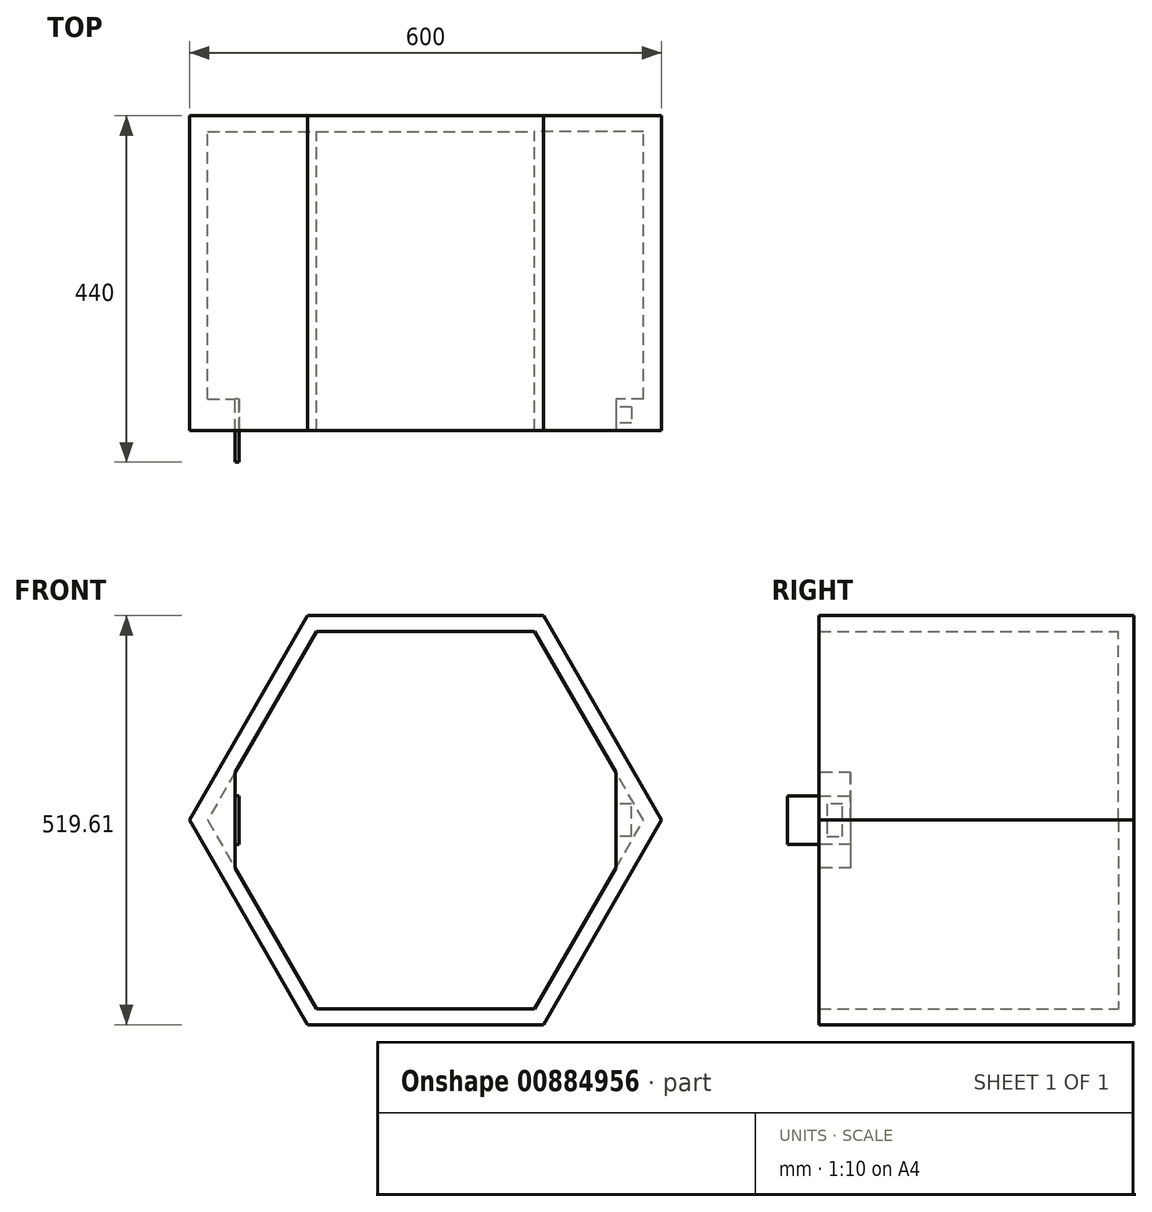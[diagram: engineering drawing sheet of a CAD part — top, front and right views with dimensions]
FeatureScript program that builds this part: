
annotation { "Feature Type Name" : "Feature", "Feature Type Description" : "" }
export const myFeature = defineFeature(function(context is Context, id is Id, definition is map)
    precondition{}
    {
        {
            var Q0;
            Q0=qCreatedBy(makeId("Front.planeOp"),FACE);
            var sketch = newSketch(context, id + "F0", { "sketchPlane" : qUnion([Q0])});
            skLineSegment(sketch, "E0", {"start": v(-124.49, 79.77) * mm, "end": v(175.51, 79.77) * mm});
            skLineSegment(sketch, "E1", {"start": v(-124.49, 79.77) * mm, "end": v(-274.49, -180.04) * mm});
            skLineSegment(sketch, "E2", {"start": v(-274.49, -180.04) * mm, "end": v(-124.49, -439.84) * mm});
            skLineSegment(sketch, "E3", {"start": v(-124.49, -439.84) * mm, "end": v(175.51, -439.84) * mm});
            skLineSegment(sketch, "E4", {"start": v(175.51, -439.84) * mm, "end": v(325.51, -180.04) * mm});
            skLineSegment(sketch, "E5", {"start": v(325.51, -180.04) * mm, "end": v(175.51, 79.77) * mm});
            skSolve(sketch);
        }
        {
            var Q0;
            Q0=makeQuery(id+"F0.imprint","IMPRINT",FACE,{"disambiguationData":[TD([[makeQuery(id+"F0.imprint","IMPRINT",EDGE,{"derivedFrom":sQuery(id+"F0.wireOp",EDGE,"E0")}),-1.0]])]});
            extrude(context, id + "F1", {"entities" : qUnion([Q0]), "depth" : 400 * mm, "offsetDistance" : 25.4 * mm});
        }
        {
            var Q0;
            Q0=makeQuery(id+"F1.opExtrude","CAP_FACE",FACE,{"disambiguationData":[OSD([sQuery(id+"F0.wireOp",EDGE,"E0"),sQuery(id+"F0.wireOp",EDGE,"E1"),sQuery(id+"F0.wireOp",EDGE,"E2"),sQuery(id+"F0.wireOp",EDGE,"E3"),sQuery(id+"F0.wireOp",EDGE,"E4"),sQuery(id+"F0.wireOp",EDGE,"E5")])],"isStart":false});
            shell(context, id + "F2", {"entities" : qUnion([Q0]), "thickness" : 20 * mm});
        }
        {
            var Q0;
            Q0=makeQuery(id+"F1.opExtrude","CAP_FACE",FACE,{"disambiguationData":[OSD([sQuery(id+"F0.wireOp",EDGE,"E0"),sQuery(id+"F0.wireOp",EDGE,"E1"),sQuery(id+"F0.wireOp",EDGE,"E2"),sQuery(id+"F0.wireOp",EDGE,"E3"),sQuery(id+"F0.wireOp",EDGE,"E4"),sQuery(id+"F0.wireOp",EDGE,"E5")])],"isStart":false});
            var sketch = newSketch(context, id + "F3", { "sketchPlane" : qUnion([Q0])});
            skLineSegment(sketch, "E6", {"start": v(-251.4, -180.04) * mm, "end": v(-216.4, -119.41) * mm});
            skLineSegment(sketch, "E7", {"start": v(-216.4, -119.41) * mm, "end": v(-216.4, -240.66) * mm});
            skLineSegment(sketch, "E8", {"start": v(-216.4, -240.66) * mm, "end": v(-251.4, -180.04) * mm});
            skLineSegment(sketch, "E9", {"start": v(302.42, -180.04) * mm, "end": v(267.42, -119.41) * mm});
            skLineSegment(sketch, "E10", {"start": v(267.42, -119.41) * mm, "end": v(267.42, -240.66) * mm});
            skLineSegment(sketch, "E11", {"start": v(267.42, -240.66) * mm, "end": v(302.42, -180.04) * mm});
            skSolve(sketch);
        }
        {
            var Q0;
            Q0=makeQuery(id+"F3.imprint","IMPRINT",FACE,{"disambiguationData":[TD([[makeQuery(id+"F3.imprint","IMPRINT",EDGE,{"derivedFrom":sQuery(id+"F3.wireOp",EDGE,"E9")}),1.0]])]});
            var Q1;
            Q1=makeQuery(id+"F3.imprint","IMPRINT",FACE,{"disambiguationData":[TD([[makeQuery(id+"F3.imprint","IMPRINT",EDGE,{"derivedFrom":sQuery(id+"F3.wireOp",EDGE,"E6")}),1.0]])]});
            extrude(context, id + "F4", {"entities" : qUnion([Q0, Q1]), "operationType" : NewBodyOperationType.ADD, "oppositeDirection" : true, "depth" : 40 * mm, "offsetDistance" : 25.4 * mm});
        }
        {
            var Q0;
            Q0=makeQuery(id+"F4.opExtrude","SWEPT_FACE",FACE,{"disambiguationData":[OSD([sQuery(id+"F3.wireOp",EDGE,"E7")])]});
            var sketch = newSketch(context, id + "F5", { "sketchPlane" : qUnion([Q0])});
            skLineSegment(sketch, "E12", {"start": v(-400, -149.41) * mm, "end": v(-360, -149.41) * mm});
            skLineSegment(sketch, "E13", {"start": v(-360, -149.41) * mm, "end": v(-360, -210.66) * mm});
            skLineSegment(sketch, "E14", {"start": v(-360, -210.66) * mm, "end": v(-400, -210.66) * mm});
            skLineSegment(sketch, "E15", {"start": v(-400, -210.66) * mm, "end": v(-400, -149.41) * mm});
            skSolve(sketch);
        }
        {
            var Q0;
            Q0 = qSketchRegion(id + "F5", true);
            extrude(context, id + "F6", {"entities" : qUnion([Q0]), "operationType" : NewBodyOperationType.ADD, "depth" : 5 * mm, "offsetDistance" : 25.4 * mm});
        }
        {
            var Q0;
            Q0=makeQuery(id+"F6.boolean.opBoolean","MERGE",FACE,{"derivedFrom":[makeQuery(id+"F4.boolean.opBoolean","MERGE",FACE,{"derivedFrom":[makeQuery(id+"F1.opExtrude","CAP_FACE",FACE,{"disambiguationData":[OSD([sQuery(id+"F0.wireOp",EDGE,"E0"),sQuery(id+"F0.wireOp",EDGE,"E1"),sQuery(id+"F0.wireOp",EDGE,"E2"),sQuery(id+"F0.wireOp",EDGE,"E3"),sQuery(id+"F0.wireOp",EDGE,"E4"),sQuery(id+"F0.wireOp",EDGE,"E5")])],"isStart":false}),makeQuery(id+"F4.opExtrude","CAP_FACE",FACE,{"disambiguationData":[OSD([sQuery(id+"F3.wireOp",EDGE,"E6"),sQuery(id+"F3.wireOp",EDGE,"E7"),sQuery(id+"F3.wireOp",EDGE,"E8")])],"isStart":true}),makeQuery(id+"F4.opExtrude","CAP_FACE",FACE,{"disambiguationData":[OSD([sQuery(id+"F3.wireOp",EDGE,"E9"),sQuery(id+"F3.wireOp",EDGE,"E10"),sQuery(id+"F3.wireOp",EDGE,"E11")])],"isStart":true})]}),makeQuery(id+"F6.opExtrude","SWEPT_FACE",FACE,{"disambiguationData":[OSD([sQuery(id+"F5.wireOp",EDGE,"E15")])]})]});
            var sketch = newSketch(context, id + "F7", { "sketchPlane" : qUnion([Q0])});
            skLineSegment(sketch, "E16", {"start": v(-211.4, -149.41) * mm, "end": v(-216.4, -149.41) * mm});
            skLineSegment(sketch, "E17", {"start": v(-216.4, -149.41) * mm, "end": v(-216.4, -210.66) * mm});
            skLineSegment(sketch, "E18", {"start": v(-216.4, -210.66) * mm, "end": v(-211.4, -210.66) * mm});
            skLineSegment(sketch, "E19", {"start": v(-211.4, -210.66) * mm, "end": v(-211.4, -149.41) * mm});
            skSolve(sketch);
        }
        {
            var Q0;
            Q0=makeQuery(id+"F7.imprint","IMPRINT",FACE,{"disambiguationData":[TD([[makeQuery(id+"F7.imprint","IMPRINT",EDGE,{"derivedFrom":sQuery(id+"F7.wireOp",EDGE,"E16")}),1.0]])]});
            extrude(context, id + "F8", {"entities" : qUnion([Q0]), "operationType" : NewBodyOperationType.ADD, "depth" : 40 * mm, "offsetDistance" : 25.4 * mm});
        }
        {
            var Q0;
            Q0=makeQuery(id+"F4.opExtrude","SWEPT_FACE",FACE,{"disambiguationData":[OSD([sQuery(id+"F3.wireOp",EDGE,"E10")])]});
            var sketch = newSketch(context, id + "F9", { "sketchPlane" : qUnion([Q0])});
            skLineSegment(sketch, "E20", {"start": v(370.09, -159.41) * mm, "end": v(390.09, -159.41) * mm});
            skLineSegment(sketch, "E21", {"start": v(390.09, -159.41) * mm, "end": v(390.09, -200.66) * mm});
            skLineSegment(sketch, "E22", {"start": v(390.09, -200.66) * mm, "end": v(370.09, -200.66) * mm});
            skLineSegment(sketch, "E23", {"start": v(370.09, -200.66) * mm, "end": v(370.09, -159.41) * mm});
            skSolve(sketch);
        }
        {
            var Q0;
            Q0 = qSketchRegion(id + "F9", true);
            extrude(context, id + "F10", {"entities" : qUnion([Q0]), "operationType" : NewBodyOperationType.REMOVE, "oppositeDirection" : true, "depth" : 20 * mm, "offsetDistance" : 25.4 * mm});
        }
    });
